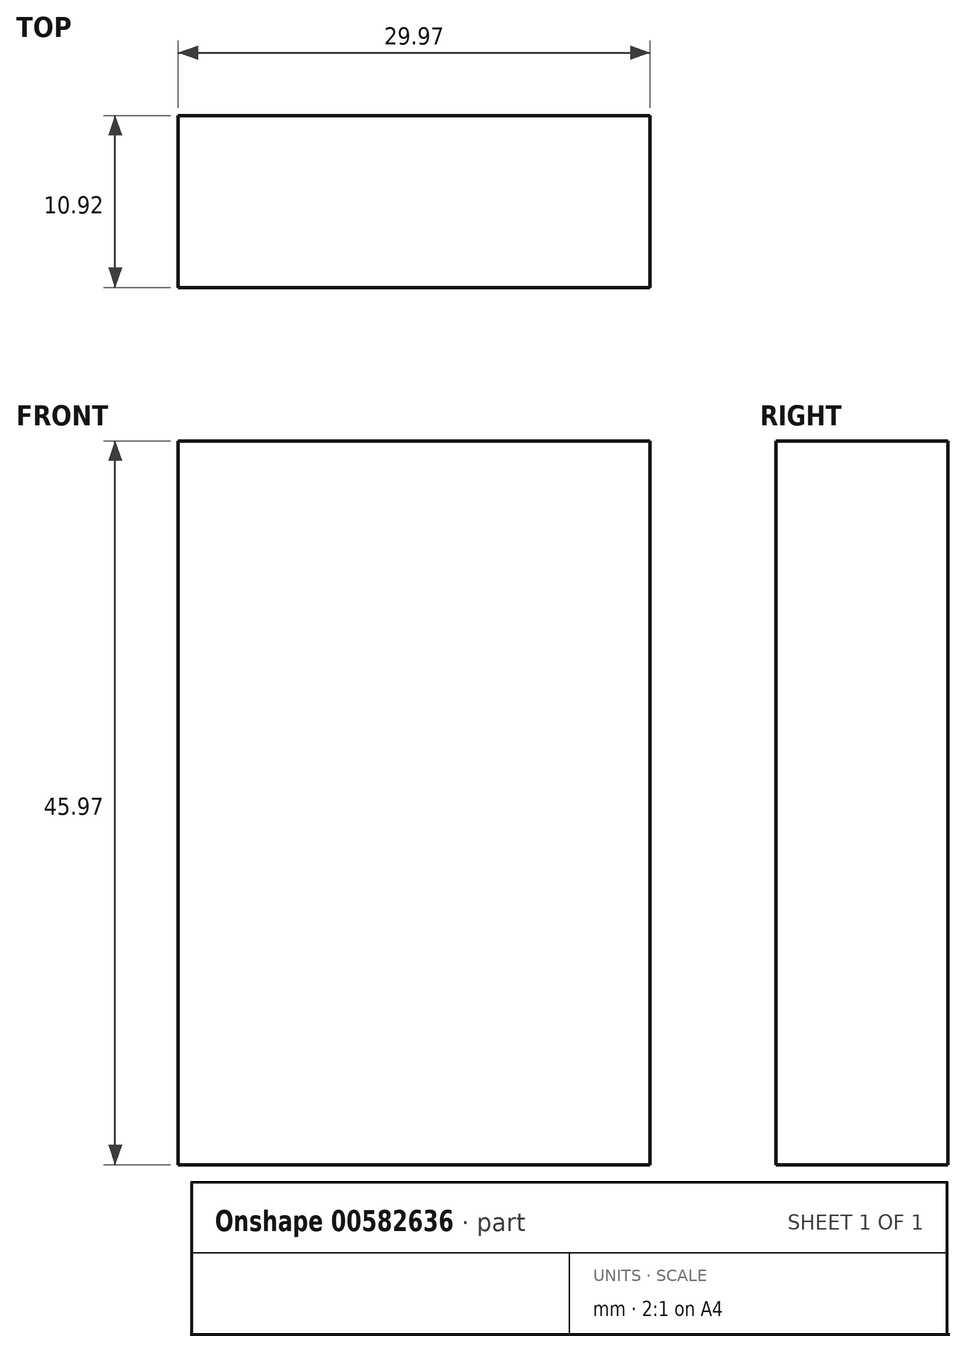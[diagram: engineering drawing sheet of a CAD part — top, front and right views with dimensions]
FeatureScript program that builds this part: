
annotation { "Feature Type Name" : "Feature", "Feature Type Description" : "" }
export const myFeature = defineFeature(function(context is Context, id is Id, definition is map)
    precondition{}
    {
        {
            var Q0;
            Q0=qCreatedBy(makeId("Front.planeOp"),FACE);
            var sketch = newSketch(context, id + "F0", { "sketchPlane" : qUnion([Q0])});
            skLineSegment(sketch, "E0.bottom", {"start": v(0, 0) * mm, "end": v(29.97, 0) * mm});
            skLineSegment(sketch, "E0.top", {"start": v(0, 45.97) * mm, "end": v(29.97, 45.97) * mm});
            skLineSegment(sketch, "E0.left", {"start": v(0, 0) * mm, "end": v(0, 45.97) * mm});
            skLineSegment(sketch, "E0.right", {"start": v(29.97, 0) * mm, "end": v(29.97, 45.97) * mm});
            skSolve(sketch);
        }
        {
            var Q0;
            Q0=makeQuery(id+"F0.imprint","IMPRINT",FACE,{"disambiguationData":[TD([[makeQuery(id+"F0.imprint","IMPRINT",EDGE,{"derivedFrom":sQuery(id+"F0.wireOp",EDGE,"E0.bottom")}),1.0]])]});
            extrude(context, id + "F1", {"entities" : qUnion([Q0]), "depth" : 10.92 * mm, "offsetDistance" : 25.4 * mm});
        }
    });
